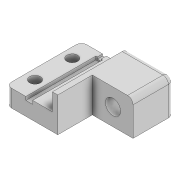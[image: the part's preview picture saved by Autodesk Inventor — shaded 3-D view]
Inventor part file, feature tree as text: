
AUTODESK INVENTOR PART (.ipt)
format: ipt  version: 2022.3 (Build 263350000, 350)  size: 241,152 bytes
history: native  units: mm
features: sketch x10, extrude x9, reference x3, other x3, plane x1, hole x1, fillet x1
ambient origin geometry x8: Origin, YZ Plane, XZ Plane, XY Plane, X Axis, Y Axis, Z Axis, Center Point
bodies: Volumenkörper1 (feature_tree)
feature tree (28):
  plane  "Arbeitsebene1"
  extrude  "Extrusion1"  TaperAngle=0.0deg  [1 undecoded]
  extrude  "Extrusion2"  Depth=15.0mm TaperAngle=0.0deg
  extrude  "Extrusion3"  Depth=17.0mm TaperAngle=0.0deg
  extrude  "Extrusion4"  Depth=1.25mm TaperAngle=0.0deg
  extrude  "Extrusion5"  Depth=0.7mm TaperAngle=0.0deg
  extrude  "Extrusion6"  Depth=25.75mm
  hole  "Bohrung1"  [1 undecoded]
  extrude  "Extrusion8"  Depth=7.0mm
  extrude  "Extrusion9"  Depth=10.0mm TaperAngle=0.0deg
  fillet  "Rundung2"  Radius=1.15mm
  extrude  "Extrusion10"  Depth=1.15mm TaperAngle=0.0deg
  sketch  "Skizze2"  dims[d1=15.0mm d2=0.0mm]
  reference  "Referenz2"
  sketch  "Skizze3"  dims[d3=15.0mm d4=15.0mm d5=0.0mm]
  reference  "Referenz3"
  sketch  "Skizze4"  dims[d6=2.0mm d7=0.0mm d8=17.0mm d9=0.0mm]
  sketch  "Skizze5"  dims[d10=2.5mm d12=1.25mm d13=0.0mm]
  sketch  "Skizze6"  dims[d14=1.4mm d15=0.7mm d16=0.0mm]
  sketch  "Skizze7"  dims[d17=25.75mm d18=4.0mm]
  sketch  "Skizze9"  dims[d19=4.0mm d20=4.0mm]
  reference  "Referenz4"
  sketch  "Skizze10"  dims[d21=4.0mm d22=7.0mm]
  sketch  "Skizze11"  dims[d23=7.0mm d24=10.0mm d25=0.0mm]
  sketch  "Skizze12"  dims[d30=5.6mm d31=6.0mm d32=9.0mm d33=6.0mm d34=90.0deg d35=15.0mm d36=0.0mm d38=1.15mm d39=0.0mm d40=1.15mm d41=0.0mm d42=2.0mm d43=5.7mm d44=3.0mm d45=0.0mm]
  other  "<userpath>\SynologyDrive\WiMi\RobotikMaschinen\HeleneRoboterarm\KraftMessNadel\Gesamt.iam"
  other  "Gesamt.iam"
  other  "micro load cell CZL635:1"
note: 2 required parameter values undecoded (feature->parameter linkage not recoverable at this tier; creation-order binding heuristic only, values carry confidence <= 0.55)
